# Revit family: agtatec_Record_SldngDrset_RST-ABST-IBST_Curtain Wall Panel
name_source: partatom
category: Curtain Panels
revit_build: Autodesk Revit Architecture 2015 (Build: 20140606_1530(x64)
units: mm (PartAtom-declared; Revit-internal decimal feet)

## types (12) — shared parameters
A = 1200 mm  [stored 3.93701 ft]
AccessoryOptions = Contact manufacturer
AlternativeDoorsetGlazing = Contact manufacturer
AntiFingerTrapRequirement = Yes
Assembly Code = B2030300
CanopyCovering = agtatec_Record_Revolving Door, Sheet metal (Painted Steel)
CanopyHeight = 220 mm  [stored 0.721785 ft]
CanopyHeightOptions = 200-1000
Category = Curved Sliding Door
Colour = Customer specific
Construction Type = Automatic Revolving Door
Description = Curved Sliding Door
Distance = 20 mm  [stored 0.0656168 ft]
DoorIncluded = Yes
DoorWingOptions = 3 wings
DoorsetOperation = automatic
DrumWallPanelFill = agtatec_Record_Revolving Door, Laminated Safety Glass (Clear)
DurationUnit = Year
ElectronicLock = Yes
Finish = Powder coated, Anodized, customer specific
FireExit = No
FloorChannel = No
FloorGuide = Yes
Flooring = agtatec_Record_Revolving Door, Felt Carpet
FrameFinishOptions = Stainless steel and more
FrameMaterial = Aluminium
FrameProfile = Aluminium
FrameSeal = Yes
GlassLayers = 1
GlassType = part of glazing spec
HandicapAccessible = No
HasDrive = Yes
HeightUnderCanopyOptions = 2200-3000
IfcExportAs = IFCDoorStyle
IfcExportType = Door
IsExternal = Yes
IssueDate = <>
LeafPanelFill = agtatec_Record_Revolving Door, Laminated Safety Glass (Clear)
ManufacturerName = record
ManufacturerURL = www.agta-record.com
Material = Aluminium
Model = K31
ModelReference = depends on the configuration
MountingProfile17mm = Yes
MountingProfile39mm = No
NBSDescription = Sliding Doorset
NBSReference = 25-50-20/175
NominalHeight = 2320 mm  [stored 7.61155 ft]
NominalLength = 1840 mm
NominalWidth = 1840 mm
OpenDoor = No
PanelFrames = agtatec_Record_Revolving Door, Aluminium
PassageHeight = 2100 mm  [stored 6.88976 ft]
PassageWidth = 1200 mm  [stored 3.93701 ft]
ProductInformation = www.agta-record.com
ReferenceStandard = EN16005, EN16361, DIN 18650, etc.
ReplacementCost = Depends on the configuration and door type
STRadius = 1200 mm  [stored 3.93701 ft]
SafetyDevices = Optical sensors
SelfClosing = Yes
ServiceLifeDuration = 10-15 years
Size = XxxXXxXX
SmokeStop = No
ThresholdRequired = Yes
TotalHeight = 2320 mm  [stored 7.61155 ft]
URL = www.agta-record.com
UnderStructure = No
Uniclass2 = Ss_25_30_20_77
Version = Version 1.0
WarrantyDescription = Depends on country
WarrantyDurationLabour = Depends on country
WarrantyDurationParts = Depends on country
WarrantyDurationUnit = Depends on country
WarrantyGuarantorLabour = Local door manufacturer
WarrantyGuarantorParts = Local door manufacturer
WithinStandardSizes = Yes
zero-valued in all types: Cost, GlassThickness1, GlassThickness2, GlassThickness3, ThermalTransmittance

## per-type parameters (varying)
| type | ABST | BIMObjectName | DiameterOptions | Features | H | IBST | Name | Panel20mm | Panel30mm | PassageWidthOptions | RST180 | RST360 | STWidth | SW | SWAdd | Shape | TFDichtung | TFWidth | W | WL | Weight | WithSidePanels | WithoutSidePanels |
| IBST With Side Panels - 20 mm | No | agtatec_Record_SldngDrset_IBST-circular-slidingDoor_WallBased |  | Air curtain | 732 mm | Yes | SldngDrset_IBST-circular-slidingDoor_Generic_Record | Yes | No | contact manufacturer | No | No | 20 mm  [stored 0.0656168 ft] | 35.28° | 3.52° | Half-Cylinder Shaped | 20 mm  [stored 0.0656168 ft] | 20 mm  [stored 0.0656168 ft] | 31.76° | 468 mm |  | Yes | No |
| IBST With Side Panels - 30 mm | No | agtatec_Record_SldngDrset_IBST-circular-slidingDoor_WallBased |  | Air curtain | 768 mm | Yes | SldngDrset_IBST-circular-slidingDoor_Generic_Record | No | Yes | contact manufacturer | No | No | 30 mm  [stored 0.0984252 ft] | 36.48° | 4.09° | Half-Cylinder Shaped | 30 mm  [stored 0.0984252 ft] | 30 mm  [stored 0.0984252 ft] | 32.39° | 432 mm  [stored 1.41732 ft] |  | Yes | No |
| ABST With Side Panels - 20 mm | Yes | agtatec_Record_SldngDrset_ABST Circular-slidingDoor_WallBased |  | Air curtain | 727 mm | No | SldngDrset_ABST Circular-slidingDoor_Generic_Record | Yes | No | contact manufacturer | No | No | 20 mm  [stored 0.0656168 ft] | 35.04° | 3.29° | Half-Cylinder Shaped | 20 mm  [stored 0.0656168 ft] | 20 mm  [stored 0.0656168 ft] | 31.76° | 473 mm |  | Yes | No |
| ABST With Side Panels - 30 mm | Yes | agtatec_Record_SldngDrset_ABST Circular-slidingDoor_WallBased |  | Air curtain | 761 mm | No | SldngDrset_ABST Circular-slidingDoor_Generic_Record | No | Yes | contact manufacturer | No | No | 30 mm  [stored 0.0984252 ft] | 36.15° | 3.76° | Half-Cylinder Shaped | 30 mm  [stored 0.0984252 ft] | 30 mm  [stored 0.0984252 ft] | 32.39° | 439 mm |  | Yes | No |
| IBST Without Side Panels - 20 mm | No | agtatec_Record_SldngDrset_IBST-circular-slidingDoor_WallBased |  | Air curtain | 732 mm | Yes | SldngDrset_IBST-circular-slidingDoor_Generic_Record | Yes | No | contact manufacturer | No | No | 20 mm  [stored 0.0656168 ft] | 35.28° | 3.52° | Half-Cylinder Shaped | 20 mm  [stored 0.0656168 ft] | 20 mm  [stored 0.0656168 ft] | 31.76° | 468 mm |  | No | Yes |
| IBST Without Side Panels - 30 mm | No | agtatec_Record_SldngDrset_IBST-circular-slidingDoor_WallBased |  | Air curtain | 768 mm | Yes | SldngDrset_IBST-circular-slidingDoor_Generic_Record | No | Yes | contact manufacturer | No | No | 30 mm  [stored 0.0984252 ft] | 36.48° | 4.09° | Half-Cylinder Shaped | 30 mm  [stored 0.0984252 ft] | 30 mm  [stored 0.0984252 ft] | 32.39° | 432 mm  [stored 1.41732 ft] |  | No | Yes |
| ABST Without Side Panels - 20 mm | Yes | agtatec_Record_SldngDrset_ABST Circular-slidingDoor_WallBased |  | Air curtain | 727 mm | No | SldngDrset_ABST Circular-slidingDoor_Generic_Record | Yes | No | contact manufacturer | No | No | 20 mm  [stored 0.0656168 ft] | 35.04° | 3.29° | Half-Cylinder Shaped | 20 mm  [stored 0.0656168 ft] | 20 mm  [stored 0.0656168 ft] | 31.76° | 473 mm |  | No | Yes |
| ABST Without Side Panels - 30 mm | Yes | agtatec_Record_SldngDrset_ABST Circular-slidingDoor_WallBased |  | Air curtain | 761 mm | No | SldngDrset_ABST Circular-slidingDoor_Generic_Record | No | Yes | contact manufacturer | No | No | 30 mm  [stored 0.0984252 ft] | 36.15° | 3.76° | Half-Cylinder Shaped | 30 mm  [stored 0.0984252 ft] | 30 mm  [stored 0.0984252 ft] | 32.39° | 439 mm |  | No | Yes |
| RST 180 - 20 mm | No | agtatec_Record_SldngDrset_RST-circular-slidingDoo_WallBased | 1500-3600 | Air curtain | 1200 mm  [stored 3.93701 ft] | No | SldngDrset_RST-circular-slidingDoor_Generic_Record | Yes | No | 1005-2451 | Yes | No | 20 mm  [stored 0.0656168 ft] | 58.24° | 3.29° | Half Cylinder Shaped | 20 mm  [stored 0.0656168 ft] | 20 mm  [stored 0.0656168 ft] | 31.76° | 0 mm  [stored 0 ft] | 160-340kg | Yes | No |
| RST 180 - 30 mm | No | agtatec_Record_SldngDrset_RST-circular-slidingDoo_WallBased | 1500-3600 | Air curtain | 1200 mm  [stored 3.93701 ft] | No | SldngDrset_RST-circular-slidingDoor_Generic_Record | No | Yes | 1005-2451 | Yes | No | 30 mm  [stored 0.0984252 ft] | 57.61° | 3.76° | Half Cylinder Shaped | 30 mm  [stored 0.0984252 ft] | 30 mm  [stored 0.0984252 ft] | 32.39° | 0 mm  [stored 0 ft] | 160-340kg | Yes | No |
| RST 360 - 20 mm | No | agtatec_Record_SldngDrset_RTS-circular-slidingDoo_WallBased | 1500-3600 | Sluice function, air curtain | 1200 mm  [stored 3.93701 ft] | No | SldngDrset_RST-circular-slidingDoor_Generic_Record | Yes | No | 1005-2451 | No | Yes | 20 mm  [stored 0.0656168 ft] | 58.24° | 3.29° | Full Cylinder Shaped | 20 mm  [stored 0.0656168 ft] | 20 mm  [stored 0.0656168 ft] | 31.76° | 0 mm  [stored 0 ft] | 320-680kg | Yes | No |
| RST 360 - 30 mm | No | agtatec_Record_SldngDrset_RTS-circular-slidingDoo_WallBased | 1500-3600 | Sluice function, air curtain | 1200 mm  [stored 3.93701 ft] | No | SldngDrset_RST-circular-slidingDoor_Generic_Record | No | Yes | 1005-2451 | No | Yes | 30 mm  [stored 0.0984252 ft] | 57.61° | 3.76° | Full Cylinder Shaped | 30 mm  [stored 0.0984252 ft] | 30 mm  [stored 0.0984252 ft] | 32.39° | 0 mm  [stored 0 ft] | 320-680kg | Yes | No |

note: [stored X ft] marks values corroborated as IEEE doubles in the binary element streams (Revit-internal decimal feet)

## geometry (parser evidence)
native form markers: Blend x8, Sweep x6
no freeform markers — native parametric forms only
